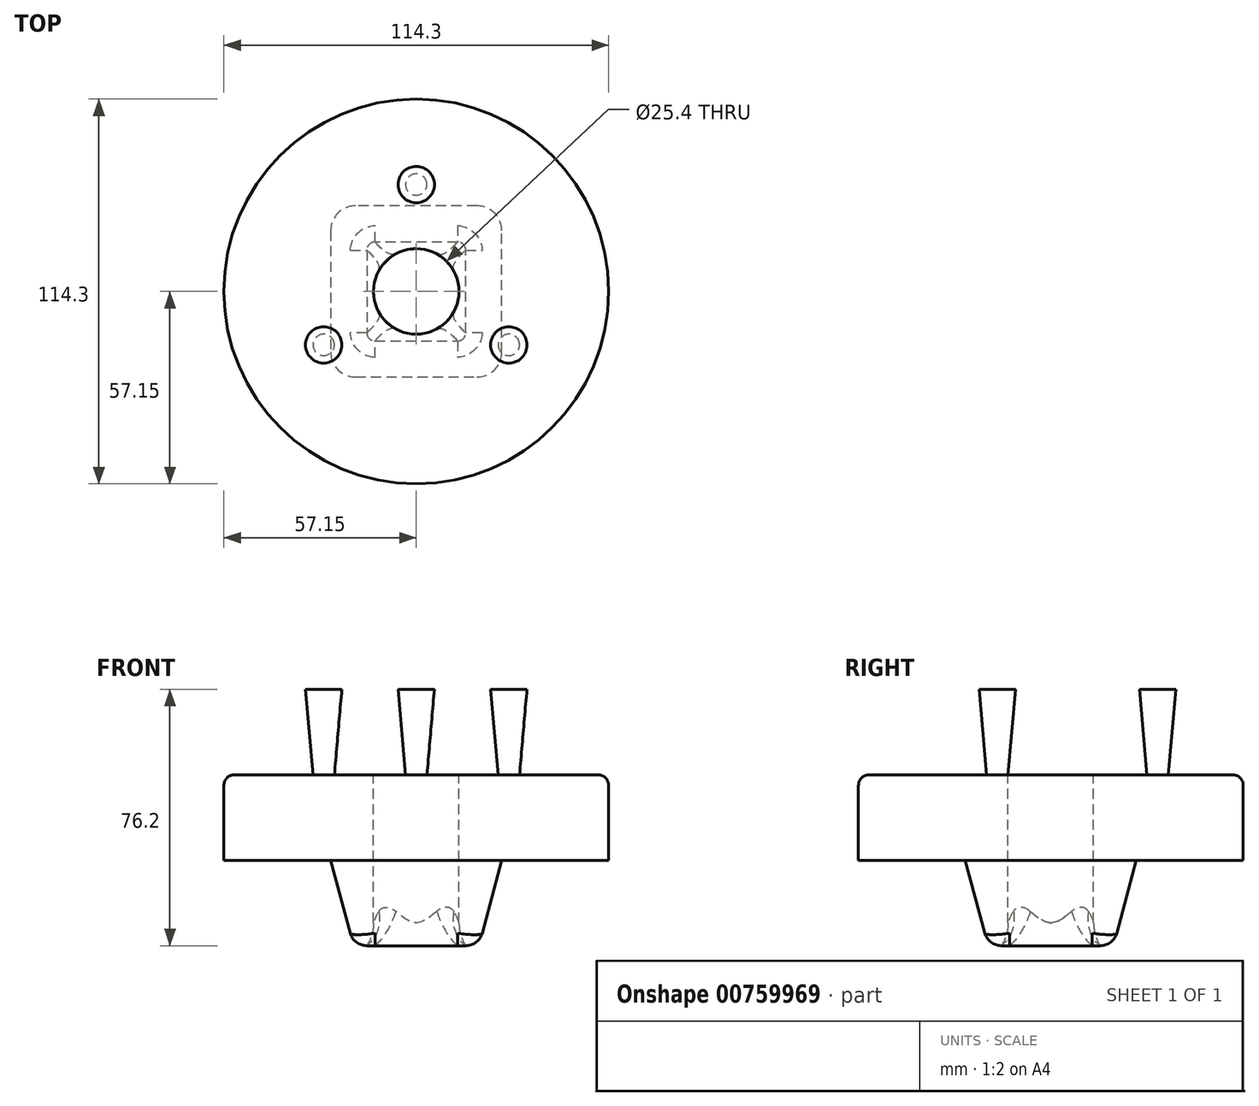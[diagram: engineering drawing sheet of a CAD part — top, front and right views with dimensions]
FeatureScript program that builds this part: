
annotation { "Feature Type Name" : "Feature", "Feature Type Description" : "" }
export const myFeature = defineFeature(function(context is Context, id is Id, definition is map)
    precondition{}
    {
        {
            var Q0;
            Q0=qCreatedBy(makeId("Top.planeOp"),FACE);
            var sketch = newSketch(context, id + "F0", { "sketchPlane" : qUnion([Q0])});
            skCircle(sketch, "E0", {"center": v(0, 0) * mm, "radius": 57.15 * mm});
            skSolve(sketch);
        }
        {
            var Q0;
            Q0=makeQuery(id+"F0.imprint","IMPRINT",FACE,{"disambiguationData":[TD([[makeQuery(id+"F0.imprint","IMPRINT",EDGE,{"derivedFrom":sQuery(id+"F0.wireOp",EDGE,"E0")}),1.0]])]});
            extrude(context, id + "F1", {"entities" : qUnion([Q0]), "depth" : 25.4 * mm, "offsetDistance" : 25.4 * mm});
        }
        {
            var Q0;
            Q0=makeQuery(id+"F1.opExtrude","CAP_FACE",FACE,{"disambiguationData":[OSD([sQuery(id+"F0.wireOp",EDGE,"E0")])],"isStart":false});
            var sketch = newSketch(context, id + "F2", { "sketchPlane" : qUnion([Q0])});
            skCircle(sketch, "E1", {"center": v(0, 0) * mm, "radius": 12.7 * mm});
            skSolve(sketch);
        }
        {
            var Q0;
            Q0=makeQuery(id+"F1.opExtrude","CAP_EDGE",EDGE,{"disambiguationData":[OSD([sQuery(id+"F0.wireOp",EDGE,"E0")])],"isStart":false});
            fillet(context, id + "F3", {"entities" : qUnion([Q0]), "radius" : 3.17 * mm, "tangentPropagation" : true, "defaultsChanged" : true, "vertexSettings" : [], "allowEdgeOverflow" : false});
        }
        {
            var Q0;
            Q0=makeQuery(id+"F1.opExtrude","CAP_FACE",FACE,{"disambiguationData":[OSD([sQuery(id+"F0.wireOp",EDGE,"E0")])],"isStart":false});
            var sketch = newSketch(context, id + "F4", { "sketchPlane" : qUnion([Q0])});
            skCircle(sketch, "E2", {"center": v(0, 31.75) * mm, "radius": 3.18 * mm});
            skCircle(sketch, "E3.1.0", {"center": v(-27.5, -15.87) * mm, "radius": 3.18 * mm});
            skCircle(sketch, "E3.2.0", {"center": v(27.5, -15.87) * mm, "radius": 3.18 * mm});
            skPoint(sketch, "E3.center", {"position": v(0, 0) * mm});
            skSolve(sketch);
        }
        {
            var Q0;
            Q0=makeQuery(id+"F4.imprint","IMPRINT",FACE,{"disambiguationData":[TD([[makeQuery(id+"F4.imprint","IMPRINT",EDGE,{"derivedFrom":sQuery(id+"F4.wireOp",EDGE,"E2")}),1.0]])]});
            var Q1;
            Q1=makeQuery(id+"F4.imprint","IMPRINT",FACE,{"disambiguationData":[TD([[makeQuery(id+"F4.imprint","IMPRINT",EDGE,{"derivedFrom":sQuery(id+"F4.wireOp",EDGE,"E3.2.0")}),1.0]])]});
            var Q2;
            Q2=makeQuery(id+"F4.imprint","IMPRINT",FACE,{"disambiguationData":[TD([[makeQuery(id+"F4.imprint","IMPRINT",EDGE,{"derivedFrom":sQuery(id+"F4.wireOp",EDGE,"E3.1.0")}),1.0]])]});
            extrude(context, id + "F5", {"entities" : qUnion([Q0, Q1, Q2]), "operationType" : NewBodyOperationType.ADD, "depth" : 25.4 * mm, "offsetDistance" : 25.4 * mm, "hasDraft" : true, "draftAngle" : 5 * degree});
        }
        {
            var Q0;
            Q0=makeQuery(id+"F0.imprint","IMPRINT",FACE,{"disambiguationData":[TD([[makeQuery(id+"F0.imprint","IMPRINT",EDGE,{"derivedFrom":sQuery(id+"F0.wireOp",EDGE,"E0")}),1.0]])]});
            var sketch = newSketch(context, id + "F6", { "sketchPlane" : qUnion([Q0])});
            skLineSegment(sketch, "E4", {"start": v(-25.4, -25.4) * mm, "end": v(25.4, -25.4) * mm});
            skLineSegment(sketch, "E5", {"start": v(25.4, -25.4) * mm, "end": v(25.4, 25.4) * mm});
            skLineSegment(sketch, "E6", {"start": v(25.4, 25.4) * mm, "end": v(-25.4, 25.4) * mm});
            skLineSegment(sketch, "E7", {"start": v(-25.4, 25.4) * mm, "end": v(-25.4, -25.4) * mm});
            skSolve(sketch);
        }
        {
            var Q0;
            Q0 = qSketchRegion(id + "F6", true);
            extrude(context, id + "F7", {"entities" : qUnion([Q0]), "operationType" : NewBodyOperationType.ADD, "oppositeDirection" : true, "depth" : 25.4 * mm, "offsetDistance" : 25.4 * mm, "hasDraft" : true, "draftAngle" : 15 * degree, "draftPullDirection" : true});
        }
        {
            var Q0;
            Q0=makeQuery(id+"F7.opExtrude","CAP_FACE",FACE,{"disambiguationData":[OSD([sQuery(id+"F6.wireOp",EDGE,"E4"),sQuery(id+"F6.wireOp",EDGE,"E5"),sQuery(id+"F6.wireOp",EDGE,"E6"),sQuery(id+"F6.wireOp",EDGE,"E7")])],"isStart":false});
            fillet(context, id + "F8", {"entities" : qUnion([Q0]), "radius" : 5.08 * mm, "tangentPropagation" : true, "allowEdgeOverflow" : false});
        }
        {
            var Q0;
            Q0=makeQuery(id+"F2.imprint","IMPRINT",FACE,{"disambiguationData":[TD([[makeQuery(id+"F2.imprint","IMPRINT",EDGE,{"derivedFrom":sQuery(id+"F2.wireOp",EDGE,"E1")}),1.0]])]});
            extrude(context, id + "F9", {"entities" : qUnion([Q0]), "operationType" : NewBodyOperationType.REMOVE, "oppositeDirection" : true, "depth" : 76.2 * mm, "offsetDistance" : 25.4 * mm});
        }
        {
            var Q0;
            Q0=makeQuery(id+"F7.opExtrude","SWEPT_EDGE",EDGE,{"disambiguationData":[OSD([sQuery(id+"F6.wireOp",EDGE,"E4"),sQuery(id+"F6.wireOp",EDGE,"E7")])]});
            var Q1;
            Q1=makeQuery(id+"F7.opExtrude","SWEPT_EDGE",EDGE,{"disambiguationData":[OSD([sQuery(id+"F6.wireOp",EDGE,"E4"),sQuery(id+"F6.wireOp",EDGE,"E5")])]});
            var Q2;
            Q2=makeQuery(id+"F7.opExtrude","SWEPT_EDGE",EDGE,{"disambiguationData":[OSD([sQuery(id+"F6.wireOp",EDGE,"E5"),sQuery(id+"F6.wireOp",EDGE,"E6")])]});
            var Q3;
            Q3=makeQuery(id+"F7.opExtrude","SWEPT_EDGE",EDGE,{"disambiguationData":[OSD([sQuery(id+"F6.wireOp",EDGE,"E6"),sQuery(id+"F6.wireOp",EDGE,"E7")])]});
            fillet(context, id + "F10", {"entities" : qUnion([Q0, Q1, Q2, Q3]), "radius" : 7.62 * mm, "tangentPropagation" : true, "allowEdgeOverflow" : false});
        }
        {
            var Q0;
            Q0=makeQuery(id+"F9.boolean.opBoolean","INTERSECT",EDGE,{"derivedFrom":[makeQuery(id+"F7.opExtrude","CAP_FACE",FACE,{"disambiguationData":[OSD([sQuery(id+"F6.wireOp",EDGE,"E4"),sQuery(id+"F6.wireOp",EDGE,"E5"),sQuery(id+"F6.wireOp",EDGE,"E6"),sQuery(id+"F6.wireOp",EDGE,"E7")])],"isStart":false}),makeQuery(id+"F9.opExtrude","SWEPT_FACE",FACE,{"disambiguationData":[OSD([sQuery(id+"F2.wireOp",EDGE,"E1")])]})]});
            fillet(context, id + "F11", {"entities" : qUnion([Q0]), "radius" : 12.7 * mm, "tangentPropagation" : true, "allowEdgeOverflow" : false});
        }
    });
